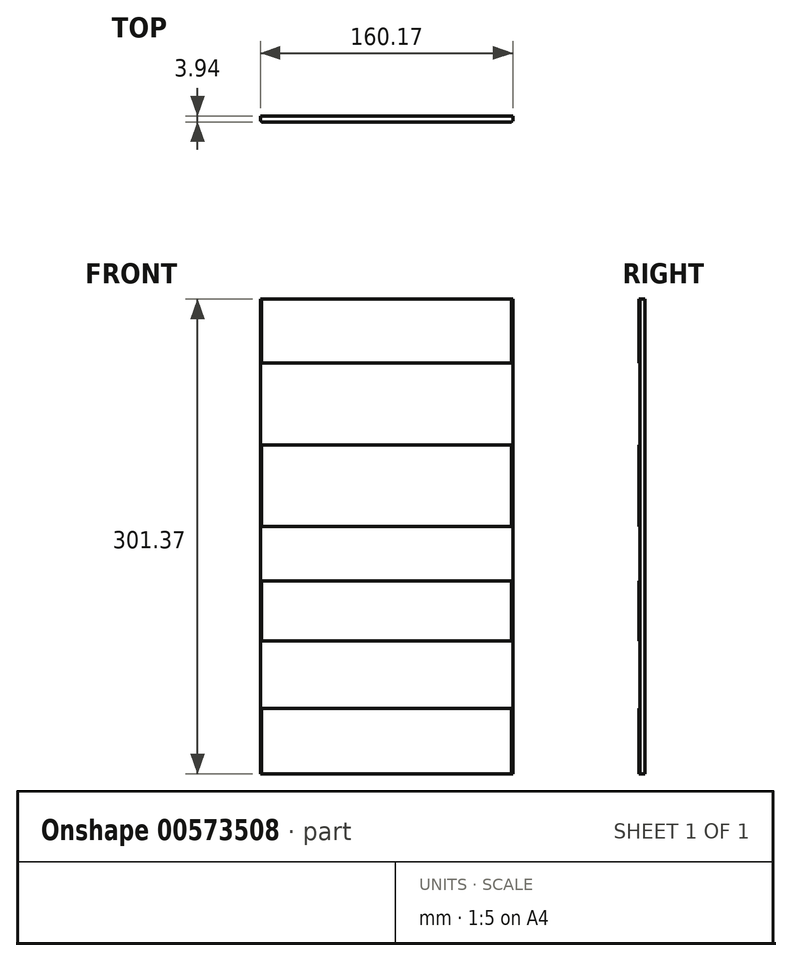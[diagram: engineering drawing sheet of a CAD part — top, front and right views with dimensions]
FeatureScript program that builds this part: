
annotation { "Feature Type Name" : "Feature", "Feature Type Description" : "" }
export const myFeature = defineFeature(function(context is Context, id is Id, definition is map)
    precondition{}
    {
        {
            var Q0;
            Q0=qCreatedBy(makeId("Front.planeOp"),FACE);
            var sketch = newSketch(context, id + "F0", { "sketchPlane" : qUnion([Q0])});
            skLineSegment(sketch, "E0.bottom", {"start": v(500.06, 0) * mm, "end": v(660.23, 0) * mm});
            skLineSegment(sketch, "E0.top", {"start": v(500.06, 301.37) * mm, "end": v(660.23, 301.37) * mm});
            skLineSegment(sketch, "E0.left", {"start": v(500.06, 0) * mm, "end": v(500.06, 301.37) * mm});
            skLineSegment(sketch, "E0.right", {"start": v(660.23, 0) * mm, "end": v(660.23, 301.37) * mm});
            skSolve(sketch);
        }
        {
            var Q0;
            Q0=makeQuery(id+"F0.imprint","IMPRINT",FACE,{"disambiguationData":[TD([[makeQuery(id+"F0.imprint","IMPRINT",EDGE,{"derivedFrom":sQuery(id+"F0.wireOp",EDGE,"E0.bottom")}),1.0]])]});
            extrude(context, id + "F1", {"entities" : qUnion([Q0]), "depth" : 3.17 * mm, "offsetDistance" : 25.4 * mm});
        }
        {
            var Q0;
            Q0=makeQuery(id+"F1.opExtrude","CAP_FACE",FACE,{"disambiguationData":[OSD([sQuery(id+"F0.wireOp",EDGE,"E0.bottom"),sQuery(id+"F0.wireOp",EDGE,"E0.top"),sQuery(id+"F0.wireOp",EDGE,"E0.left"),sQuery(id+"F0.wireOp",EDGE,"E0.right")])],"isStart":false});
            var sketch = newSketch(context, id + "F2", { "sketchPlane" : qUnion([Q0])});
            skLineSegment(sketch, "E1.bottom", {"start": v(500.77, 41.4) * mm, "end": v(659.52, 41.4) * mm});
            skLineSegment(sketch, "E1.top", {"start": v(500.77, 0) * mm, "end": v(659.52, 0) * mm});
            skLineSegment(sketch, "E1.left", {"start": v(500.77, 41.4) * mm, "end": v(500.77, 0) * mm});
            skLineSegment(sketch, "E1.right", {"start": v(659.52, 41.4) * mm, "end": v(659.52, 0) * mm});
            skPoint(sketch, "E2", {"position": v(580.15, 0) * mm});
            skLineSegment(sketch, "E3.bottom", {"start": v(500.06, 83.95) * mm, "end": v(660.23, 83.95) * mm});
            skLineSegment(sketch, "E3.top", {"start": v(500.06, 41.66) * mm, "end": v(660.23, 41.66) * mm});
            skLineSegment(sketch, "E3.left", {"start": v(500.06, 83.95) * mm, "end": v(500.06, 41.66) * mm});
            skLineSegment(sketch, "E3.right", {"start": v(660.23, 83.95) * mm, "end": v(660.23, 41.66) * mm});
            skPoint(sketch, "E4", {"position": v(580.15, 41.66) * mm});
            skLineSegment(sketch, "E5.bottom", {"start": v(500.77, 122.3) * mm, "end": v(659.52, 122.3) * mm});
            skLineSegment(sketch, "E5.top", {"start": v(500.77, 84.2) * mm, "end": v(659.52, 84.2) * mm});
            skLineSegment(sketch, "E5.left", {"start": v(500.77, 122.3) * mm, "end": v(500.77, 84.2) * mm});
            skLineSegment(sketch, "E5.right", {"start": v(659.52, 122.3) * mm, "end": v(659.52, 84.2) * mm});
            skLineSegment(sketch, "E6.bottom", {"start": v(499.88, 156.84) * mm, "end": v(660.41, 156.84) * mm});
            skLineSegment(sketch, "E6.top", {"start": v(499.88, 122.56) * mm, "end": v(660.41, 122.56) * mm});
            skLineSegment(sketch, "E6.left", {"start": v(499.88, 156.84) * mm, "end": v(499.88, 122.55) * mm});
            skLineSegment(sketch, "E6.right", {"start": v(660.41, 156.84) * mm, "end": v(660.41, 122.55) * mm});
            skPoint(sketch, "E7", {"position": v(580.15, 84.2) * mm});
            skPoint(sketch, "E8", {"position": v(580.15, 122.55) * mm});
            skLineSegment(sketch, "E9.bottom", {"start": v(500.77, 301.37) * mm, "end": v(659.52, 301.37) * mm});
            skLineSegment(sketch, "E9.top", {"start": v(500.77, 260.73) * mm, "end": v(659.52, 260.73) * mm});
            skLineSegment(sketch, "E9.left", {"start": v(500.77, 301.37) * mm, "end": v(500.77, 260.73) * mm});
            skLineSegment(sketch, "E9.right", {"start": v(659.52, 301.37) * mm, "end": v(659.52, 260.73) * mm});
            skLineSegment(sketch, "E10.bottom", {"start": v(500.77, 260.48) * mm, "end": v(659.52, 260.48) * mm});
            skLineSegment(sketch, "E10.top", {"start": v(500.77, 208.91) * mm, "end": v(659.52, 208.91) * mm});
            skLineSegment(sketch, "E10.left", {"start": v(500.77, 260.48) * mm, "end": v(500.77, 208.91) * mm});
            skLineSegment(sketch, "E10.right", {"start": v(659.52, 260.48) * mm, "end": v(659.52, 208.91) * mm});
            skLineSegment(sketch, "E11.bottom", {"start": v(500.77, 208.66) * mm, "end": v(659.52, 208.66) * mm});
            skLineSegment(sketch, "E11.top", {"start": v(500.77, 157.1) * mm, "end": v(659.52, 157.1) * mm});
            skLineSegment(sketch, "E11.left", {"start": v(500.77, 208.66) * mm, "end": v(500.77, 157.1) * mm});
            skLineSegment(sketch, "E11.right", {"start": v(659.52, 208.66) * mm, "end": v(659.52, 157.1) * mm});
            skPoint(sketch, "E12", {"position": v(580.15, 260.73) * mm});
            skPoint(sketch, "E13", {"position": v(580.15, 208.91) * mm});
            skPoint(sketch, "E14", {"position": v(580.15, 157.1) * mm});
            skSolve(sketch);
        }
        {
            var Q0;
            Q0=makeQuery(id+"F2.imprint","IMPRINT",FACE,{"disambiguationData":[TD([[makeQuery(id+"F2.imprint","IMPRINT",EDGE,{"derivedFrom":sQuery(id+"F2.wireOp",EDGE,"E9.bottom")}),-1.0]])]});
            var Q1;
            Q1=makeQuery(id+"F2.imprint","IMPRINT",FACE,{"disambiguationData":[TD([[makeQuery(id+"F2.imprint","IMPRINT",EDGE,{"derivedFrom":sQuery(id+"F2.wireOp",EDGE,"E11.bottom")}),-1.0]])]});
            var Q2;
            Q2=makeQuery(id+"F2.imprint","IMPRINT",FACE,{"disambiguationData":[TD([[makeQuery(id+"F2.imprint","IMPRINT",EDGE,{"derivedFrom":sQuery(id+"F2.wireOp",EDGE,"E5.bottom")}),-1.0]])]});
            var Q3;
            Q3=makeQuery(id+"F2.imprint","IMPRINT",FACE,{"disambiguationData":[TD([[makeQuery(id+"F2.imprint","IMPRINT",EDGE,{"derivedFrom":sQuery(id+"F2.wireOp",EDGE,"E1.bottom")}),-1.0]])]});
            extrude(context, id + "F3", {"entities" : qUnion([Q0, Q1, Q2, Q3]), "operationType" : NewBodyOperationType.ADD, "depth" : 0.76 * mm, "offsetDistance" : 25.4 * mm});
        }
    });
